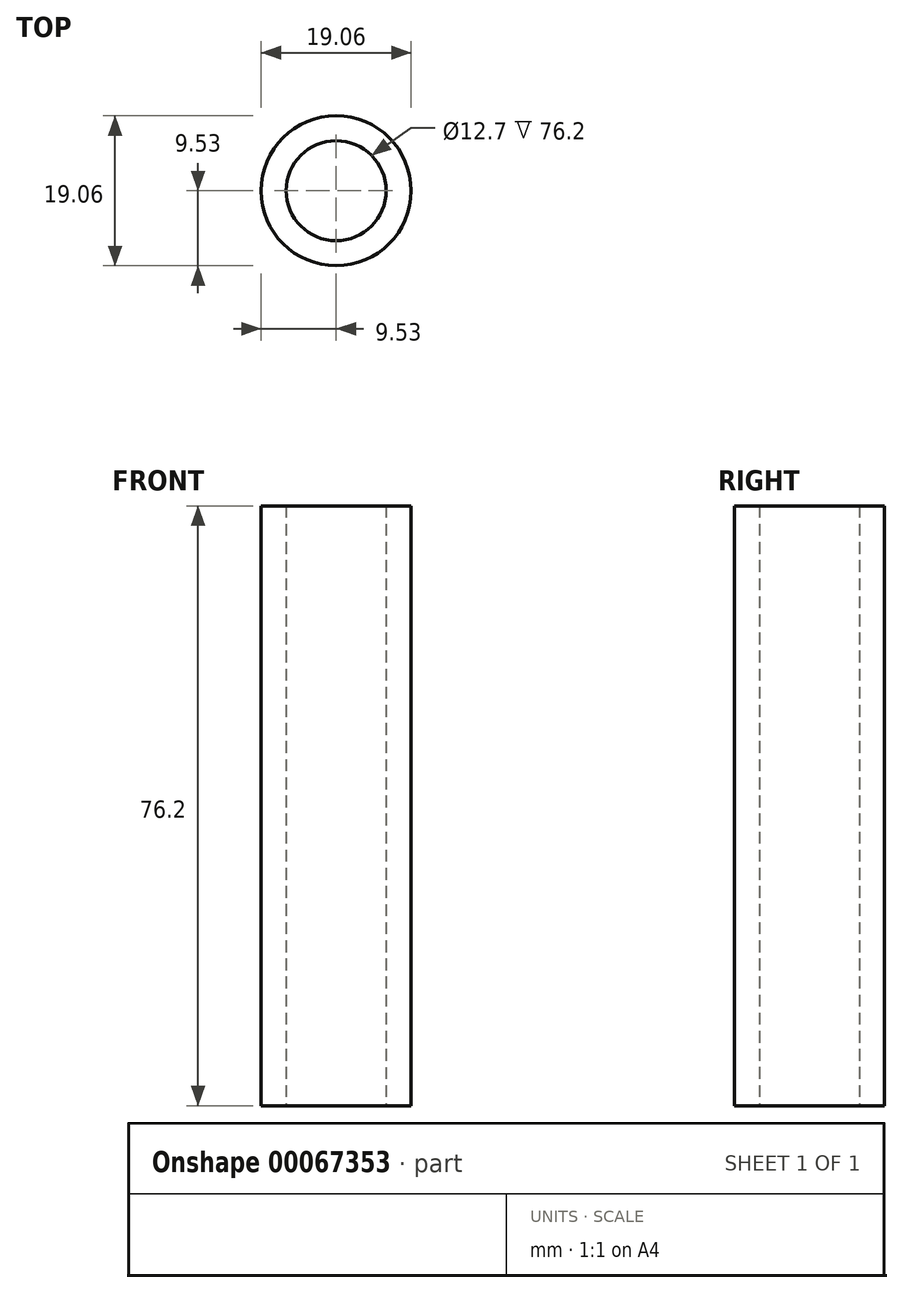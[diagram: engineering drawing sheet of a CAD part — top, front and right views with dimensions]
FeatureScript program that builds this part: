
annotation { "Feature Type Name" : "Feature", "Feature Type Description" : "" }
export const myFeature = defineFeature(function(context is Context, id is Id, definition is map)
    precondition{}
    {
        {
            var Q0;
            Q0=qCreatedBy(makeId("Top.planeOp"),FACE);
            var sketch = newSketch(context, id + "F0", { "sketchPlane" : qUnion([Q0])});
            skCircle(sketch, "E0", {"center": v(0, 0) * mm, "radius": 6.35 * mm});
            skCircle(sketch, "E1", {"center": v(0, 0) * mm, "radius": 9.53 * mm});
            skSolve(sketch);
        }
        {
            var Q0;
            Q0 = qSketchRegion(id + "F0", true);
            extrude(context, id + "F1", {"entities" : qUnion([Q0]), "depth" : 76.2 * mm});
        }
    });
